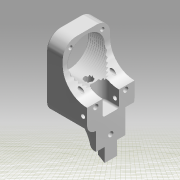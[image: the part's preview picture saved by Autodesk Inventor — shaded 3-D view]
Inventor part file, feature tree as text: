
AUTODESK INVENTOR PART (.ipt)
format: ipt  version: 2018 (Build 220112000, 112)  size: 652,800 bytes
history: native  units: mm (DEFAULTED — no unit token found)
features: extrude x1, sketch x1, imported_body x1
ambient origin geometry x8: Origin, YZ Plane, XZ Plane, XY Plane, X Axis, Y Axis, Z Axis, Center Point
bodies: Solid1 (feature_tree)
feature tree (3):
  extrude  "Extrusion1"  [1 undecoded]
  sketch  "Sketch1"  dims[d0=25.4mm d1=0.0mm]
  imported_body  "Base1"
note: 1 required parameter value undecoded (feature->parameter linkage not recoverable at this tier; creation-order binding heuristic only, values carry confidence <= 0.55)
